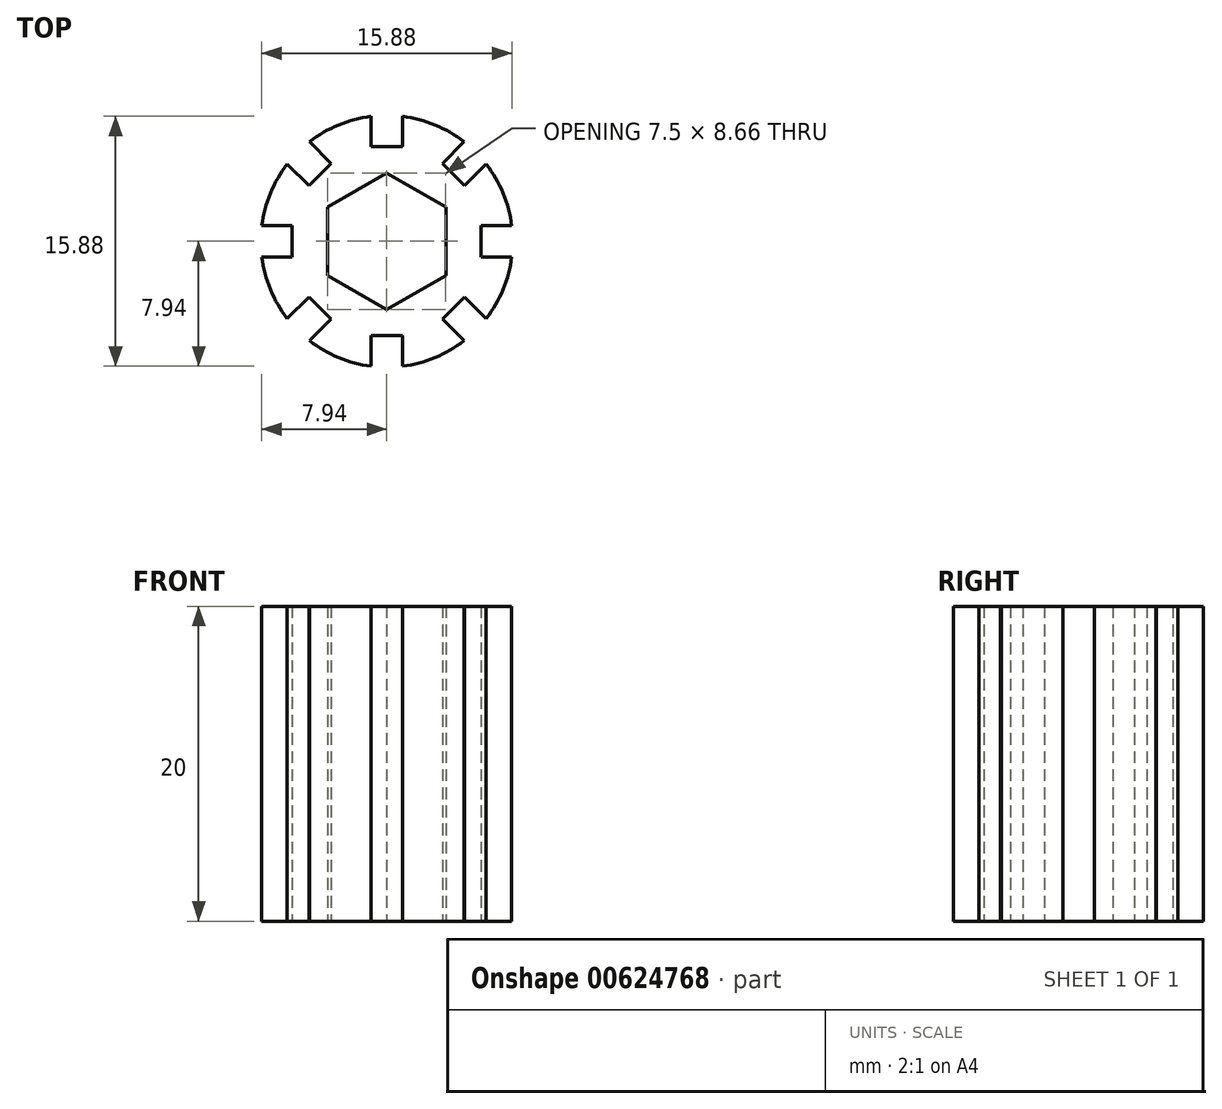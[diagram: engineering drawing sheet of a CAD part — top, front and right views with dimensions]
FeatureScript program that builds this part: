
annotation { "Feature Type Name" : "Feature", "Feature Type Description" : "" }
export const myFeature = defineFeature(function(context is Context, id is Id, definition is map)
    precondition{}
    {
        {
            var Q0;
            Q0=qCreatedBy(makeId("Top.planeOp"),FACE);
            var sketch = newSketch(context, id + "F0", { "sketchPlane" : qUnion([Q0])});
            skCircle(sketch, "E0", {"center": v(0, 0) * mm, "radius": 8 * mm, "construction": true});
            skLineSegment(sketch, "E1", {"start": v(0, 8) * mm, "end": v(0, -8) * mm, "construction": true});
            skLineSegment(sketch, "E2", {"start": v(-8, 0) * mm, "end": v(8, 0) * mm, "construction": true});
            skLineSegment(sketch, "E3", {"start": v(5.66, 5.66) * mm, "end": v(-5.66, -5.66) * mm, "construction": true});
            skLineSegment(sketch, "E4", {"start": v(-5.66, 5.66) * mm, "end": v(5.66, -5.66) * mm, "construction": true});
            skSolve(sketch);
        }
        {
            var Q0;
            Q0=qCreatedBy(makeId("Top.planeOp"),FACE);
            var sketch = newSketch(context, id + "F1", { "sketchPlane" : qUnion([Q0])});
            skArc(sketch, "E5.0", {"start": v(-1, 7.94) * mm, "mid": v(-3.06, 7.4) * mm, "end": v(-4.9, 6.32) * mm, "construction": true});
            skCircle(sketch, "E6.cCircle", {"center": v(0, 0) * mm, "radius": 3.75 * mm, "construction": true});
            skLineSegment(sketch, "E6.0", {"start": v(0, 4.33) * mm, "end": v(3.75, 2.17) * mm});
            skLineSegment(sketch, "E6.1", {"start": v(3.75, 2.17) * mm, "end": v(3.75, -2.17) * mm});
            skLineSegment(sketch, "E6.2", {"start": v(3.75, -2.17) * mm, "end": v(0, -4.33) * mm});
            skLineSegment(sketch, "E6.3", {"start": v(0, -4.33) * mm, "end": v(-3.75, -2.17) * mm});
            skLineSegment(sketch, "E6.4", {"start": v(-3.75, -2.17) * mm, "end": v(-3.75, 2.17) * mm});
            skLineSegment(sketch, "E6.5", {"start": v(-3.75, 2.17) * mm, "end": v(0, 4.33) * mm});
            skPoint(sketch, "E6.0.midPoint", {"position": v(1.87, 3.25) * mm});
            skLineSegment(sketch, "E7", {"start": v(-1, 7.94) * mm, "end": v(-1, 6) * mm});
            skLineSegment(sketch, "E8", {"start": v(-1, 6) * mm, "end": v(1, 6) * mm});
            skLineSegment(sketch, "E9", {"start": v(1, 6) * mm, "end": v(1, 7.94) * mm});
            skLineSegment(sketch, "E10.1.0", {"start": v(-6.32, 4.9) * mm, "end": v(-4.95, 3.54) * mm});
            skLineSegment(sketch, "E10.1.1", {"start": v(-4.95, 3.54) * mm, "end": v(-3.54, 4.95) * mm});
            skLineSegment(sketch, "E10.1.2", {"start": v(-3.54, 4.95) * mm, "end": v(-4.9, 6.32) * mm});
            skLineSegment(sketch, "E10.2.0", {"start": v(-7.94, -1) * mm, "end": v(-6, -1) * mm});
            skLineSegment(sketch, "E10.2.1", {"start": v(-6, -1) * mm, "end": v(-6, 1) * mm});
            skLineSegment(sketch, "E10.2.2", {"start": v(-6, 1) * mm, "end": v(-7.94, 1) * mm});
            skLineSegment(sketch, "E10.3.0", {"start": v(-4.9, -6.32) * mm, "end": v(-3.54, -4.95) * mm});
            skLineSegment(sketch, "E10.3.1", {"start": v(-3.54, -4.95) * mm, "end": v(-4.95, -3.54) * mm});
            skLineSegment(sketch, "E10.3.2", {"start": v(-4.95, -3.54) * mm, "end": v(-6.32, -4.9) * mm});
            skLineSegment(sketch, "E10.4.0", {"start": v(1, -7.94) * mm, "end": v(1, -6) * mm});
            skLineSegment(sketch, "E10.4.1", {"start": v(1, -6) * mm, "end": v(-1, -6) * mm});
            skLineSegment(sketch, "E10.4.2", {"start": v(-1, -6) * mm, "end": v(-1, -7.94) * mm});
            skLineSegment(sketch, "E10.5.0", {"start": v(6.32, -4.9) * mm, "end": v(4.95, -3.54) * mm});
            skLineSegment(sketch, "E10.5.1", {"start": v(4.95, -3.54) * mm, "end": v(3.54, -4.95) * mm});
            skLineSegment(sketch, "E10.5.2", {"start": v(3.54, -4.95) * mm, "end": v(4.9, -6.32) * mm});
            skLineSegment(sketch, "E10.6.0", {"start": v(7.94, 1) * mm, "end": v(6, 1) * mm});
            skLineSegment(sketch, "E10.6.1", {"start": v(6, 1) * mm, "end": v(6, -1) * mm});
            skLineSegment(sketch, "E10.6.2", {"start": v(6, -1) * mm, "end": v(7.94, -1) * mm});
            skLineSegment(sketch, "E10.7.0", {"start": v(4.9, 6.32) * mm, "end": v(3.54, 4.95) * mm});
            skLineSegment(sketch, "E10.7.1", {"start": v(3.54, 4.95) * mm, "end": v(4.95, 3.54) * mm});
            skLineSegment(sketch, "E10.7.2", {"start": v(4.95, 3.54) * mm, "end": v(6.32, 4.9) * mm});
            skArc(sketch, "E11", {"start": v(-1, 7.94) * mm, "mid": v(-3.06, 7.4) * mm, "end": v(-4.9, 6.32) * mm});
            skArc(sketch, "E12.trimOffspring", {"start": v(-6.32, 4.9) * mm, "mid": v(-7.4, 3.06) * mm, "end": v(-7.94, 1) * mm, "construction": true});
            skArc(sketch, "E13.trimOffspring", {"start": v(-7.94, -1) * mm, "mid": v(-7.4, -3.06) * mm, "end": v(-6.32, -4.9) * mm, "construction": true});
            skArc(sketch, "E14.trimOffspring", {"start": v(-4.9, -6.32) * mm, "mid": v(-3.06, -7.4) * mm, "end": v(-1, -7.94) * mm, "construction": true});
            skArc(sketch, "E15.trimOffspring", {"start": v(1, -7.94) * mm, "mid": v(3.06, -7.4) * mm, "end": v(4.9, -6.32) * mm, "construction": true});
            skArc(sketch, "E16.trimOffspring", {"start": v(6.32, -4.9) * mm, "mid": v(7.4, -3.06) * mm, "end": v(7.94, -1) * mm, "construction": true});
            skArc(sketch, "E17.trimOffspring", {"start": v(7.94, 1) * mm, "mid": v(7.4, 3.06) * mm, "end": v(6.32, 4.9) * mm, "construction": true});
            skArc(sketch, "E18.trimOffspring", {"start": v(4.9, 6.32) * mm, "mid": v(3.06, 7.4) * mm, "end": v(1, 7.94) * mm, "construction": true});
            skArc(sketch, "E19.trimOffspring", {"start": v(-6.32, 4.9) * mm, "mid": v(-7.4, 3.06) * mm, "end": v(-7.94, 1) * mm});
            skArc(sketch, "E20.trimOffspring", {"start": v(-7.94, -1) * mm, "mid": v(-7.4, -3.06) * mm, "end": v(-6.32, -4.9) * mm});
            skArc(sketch, "E21.trimOffspring", {"start": v(-4.9, -6.32) * mm, "mid": v(-3.06, -7.4) * mm, "end": v(-1, -7.94) * mm});
            skArc(sketch, "E22.trimOffspring", {"start": v(1, -7.94) * mm, "mid": v(3.06, -7.4) * mm, "end": v(4.9, -6.32) * mm});
            skArc(sketch, "E23.trimOffspring", {"start": v(6.32, -4.9) * mm, "mid": v(7.4, -3.06) * mm, "end": v(7.94, -1) * mm});
            skArc(sketch, "E24.trimOffspring", {"start": v(7.94, 1) * mm, "mid": v(7.4, 3.06) * mm, "end": v(6.32, 4.9) * mm});
            skArc(sketch, "E25.trimOffspring", {"start": v(4.9, 6.32) * mm, "mid": v(3.06, 7.4) * mm, "end": v(1, 7.94) * mm});
            skSolve(sketch);
        }
        {
            var Q0;
            Q0=makeQuery(id+"F1.imprint","IMPRINT",FACE,{"disambiguationData":[TD([[makeQuery(id+"F1.imprint","IMPRINT",EDGE,{"derivedFrom":sQuery(id+"F1.wireOp",EDGE,"E6.0")}),1.0]])]});
            extrude(context, id + "F2", {"entities" : qUnion([Q0]), "depth" : 20 * mm, "offsetDistance" : 25 * mm});
        }
    });
